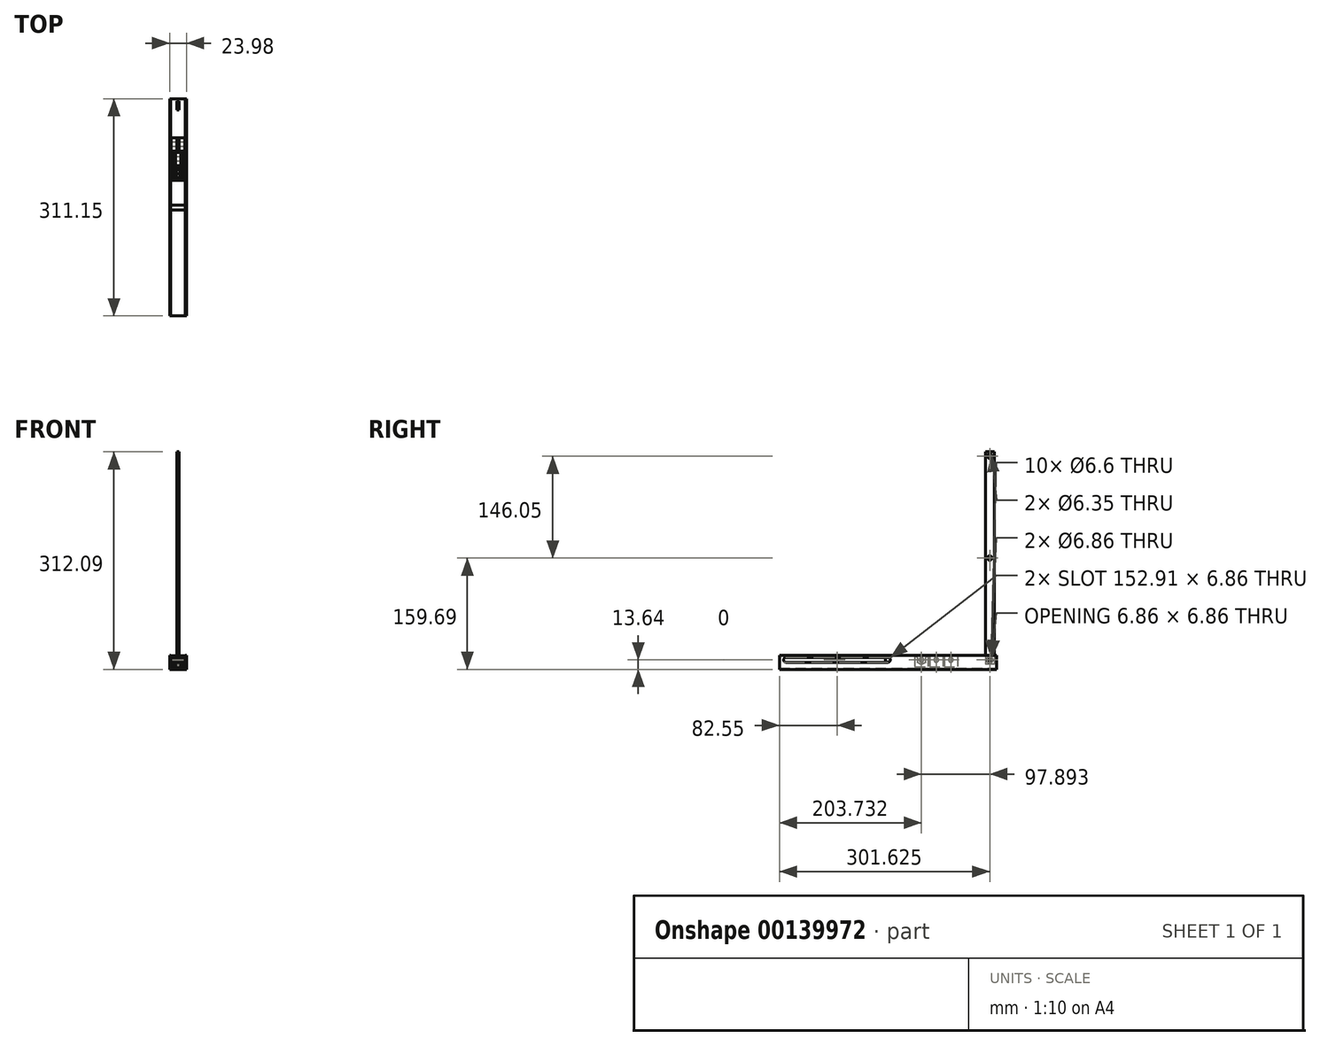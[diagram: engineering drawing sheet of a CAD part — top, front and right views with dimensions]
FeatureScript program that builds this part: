
annotation { "Feature Type Name" : "Feature", "Feature Type Description" : "" }
export const myFeature = defineFeature(function(context is Context, id is Id, definition is map)
    precondition{}
    {
        {
            var Q0;
            Q0=qCreatedBy(makeId("Front.planeOp"),FACE);
            var sketch = newSketch(context, id + "F0", { "sketchPlane" : qUnion([Q0])});
            skLineSegment(sketch, "E0", {"start": v(-11.99, 0) * mm, "end": v(11.99, 0) * mm});
            skLineSegment(sketch, "E1", {"start": v(11.99, 0) * mm, "end": v(11.99, 19.99) * mm});
            skLineSegment(sketch, "E2", {"start": v(11.99, 19.99) * mm, "end": v(10.31, 19.99) * mm});
            skLineSegment(sketch, "E3", {"start": v(10.31, 19.99) * mm, "end": v(10.31, 1.68) * mm});
            skLineSegment(sketch, "E4", {"start": v(10.31, 1.68) * mm, "end": v(-10.31, 1.68) * mm});
            skLineSegment(sketch, "E5", {"start": v(-10.31, 1.68) * mm, "end": v(-10.31, 19.99) * mm});
            skLineSegment(sketch, "E6", {"start": v(-10.31, 19.99) * mm, "end": v(-11.99, 19.99) * mm});
            skLineSegment(sketch, "E7", {"start": v(-11.99, 19.99) * mm, "end": v(-11.99, 0) * mm});
            skLineSegment(sketch, "E8", {"start": v(0, 0) * mm, "end": v(0, 10.38) * mm, "construction": true});
            skSolve(sketch);
        }
        {
            var Q0;
            Q0 = qSketchRegion(id + "F0", true);
            extrude(context, id + "F1", {"entities" : qUnion([Q0]), "depth" : 311.15 * mm});
        }
        {
            var Q0;
            Q0=qCreatedBy(makeId("Right.planeOp"),FACE);
            var sketch = newSketch(context, id + "F2", { "sketchPlane" : qUnion([Q0])});
            skCircle(sketch, "E9", {"center": v(-9.53, 13.64) * mm, "radius": 3.43 * mm});
            skArc(sketch, "E10", {"start": v(-155.58, 10.21) * mm, "mid": v(-152.15, 13.66) * mm, "end": v(-155.62, 17.07) * mm});
            skArc(sketch, "E11", {"start": v(-301.62, 17.07) * mm, "mid": v(-305.05, 13.64) * mm, "end": v(-301.62, 10.21) * mm});
            skLineSegment(sketch, "E12", {"start": v(-301.63, 13.64) * mm, "end": v(-155.58, 13.64) * mm, "construction": true});
            skLineSegment(sketch, "E13", {"start": v(-155.53, 17.07) * mm, "end": v(-301.62, 17.07) * mm});
            skLineSegment(sketch, "E14", {"start": v(-301.62, 10.21) * mm, "end": v(-155.58, 10.21) * mm});
            skSolve(sketch);
        }
        {
            var Q0;
            Q0 = qSketchRegion(id + "F2", true);
            extrude(context, id + "F3", {"entities" : qUnion([Q0]), "operationType" : NewBodyOperationType.REMOVE, "endBound" : BoundingType.THROUGH_ALL, "oppositeDirection" : true, "depth" : 25.4 * mm, "hasSecondDirection" : true, "secondDirectionBound" : SecondDirectionBoundingType.THROUGH_ALL, "secondDirectionOppositeDirection" : false, "secondDirectionDepth" : 25.4 * mm});
        }
        {
            var Q0;
            Q0=makeQuery(id+"F1.opExtrude","CAP_FACE",FACE,{"disambiguationData":[OSD([sQuery(id+"F0.wireOp",EDGE,"E0"),sQuery(id+"F0.wireOp",EDGE,"E1"),sQuery(id+"F0.wireOp",EDGE,"E2"),sQuery(id+"F0.wireOp",EDGE,"E3"),sQuery(id+"F0.wireOp",EDGE,"E4"),sQuery(id+"F0.wireOp",EDGE,"E5"),sQuery(id+"F0.wireOp",EDGE,"E6"),sQuery(id+"F0.wireOp",EDGE,"E7")])],"isStart":true});
            var sketch = newSketch(context, id + "F4", { "sketchPlane" : qUnion([Q0])});
            skLineSegment(sketch, "E15.0", {"start": v(9.8, 2.18) * mm, "end": v(9.8, 19.99) * mm});
            skLineSegment(sketch, "E15.1", {"start": v(-9.8, 2.18) * mm, "end": v(9.8, 2.18) * mm});
            skLineSegment(sketch, "E15.2", {"start": v(-9.8, 19.99) * mm, "end": v(-9.8, 2.18) * mm});
            skLineSegment(sketch, "E16", {"start": v(-9.8, 19.48) * mm, "end": v(9.8, 19.48) * mm});
            skLineSegment(sketch, "E17", {"start": v(-10.31, 19.99) * mm, "end": v(-9.8, 19.99) * mm});
            skLineSegment(sketch, "E18.trimOffspring", {"start": v(9.8, 19.99) * mm, "end": v(10.31, 19.99) * mm});
            skLineSegment(sketch, "E19", {"start": v(0, 3.7) * mm, "end": v(0, 19.48) * mm});
            skPoint(sketch, "E19.startSnap0", {"position": v(0, 19.48) * mm});
            skLineSegment(sketch, "E20", {"start": v(5.46, 19.48) * mm, "end": v(5.46, 3.7) * mm});
            skLineSegment(sketch, "E21", {"start": v(5.46, 3.7) * mm, "end": v(-5.46, 3.7) * mm});
            skLineSegment(sketch, "E22", {"start": v(-5.46, 3.7) * mm, "end": v(-5.46, 19.48) * mm});
            skLineSegment(sketch, "E23.bottom", {"start": v(-3.8, 19.48) * mm, "end": v(-7.11, 19.48) * mm});
            skLineSegment(sketch, "E23.top", {"start": v(-3.8, 3.7) * mm, "end": v(-7.11, 3.7) * mm});
            skLineSegment(sketch, "E23.left", {"start": v(-3.8, 19.48) * mm, "end": v(-3.8, 3.7) * mm});
            skLineSegment(sketch, "E23.right", {"start": v(-7.11, 19.48) * mm, "end": v(-7.11, 3.7) * mm});
            skPoint(sketch, "E23.middle", {"position": v(-5.46, 11.6) * mm});
            skLineSegment(sketch, "E24.bottom", {"start": v(-1.65, 19.48) * mm, "end": v(1.65, 19.48) * mm});
            skLineSegment(sketch, "E24.top", {"start": v(-1.65, 3.7) * mm, "end": v(1.65, 3.7) * mm});
            skLineSegment(sketch, "E24.left", {"start": v(-1.65, 19.48) * mm, "end": v(-1.65, 3.7) * mm});
            skLineSegment(sketch, "E24.right", {"start": v(1.65, 19.48) * mm, "end": v(1.65, 3.7) * mm});
            skPoint(sketch, "E24.middle", {"position": v(0, 11.6) * mm});
            skLineSegment(sketch, "E25.bottom", {"start": v(3.81, 19.48) * mm, "end": v(7.11, 19.48) * mm});
            skLineSegment(sketch, "E25.top", {"start": v(3.81, 3.7) * mm, "end": v(7.11, 3.7) * mm});
            skLineSegment(sketch, "E25.left", {"start": v(3.81, 19.48) * mm, "end": v(3.81, 3.7) * mm});
            skLineSegment(sketch, "E25.right", {"start": v(7.11, 19.48) * mm, "end": v(7.11, 3.7) * mm});
            skPoint(sketch, "E25.middle", {"position": v(5.46, 11.6) * mm});
            skSolve(sketch);
        }
        {
            var Q0;
            {var subQ0=sQuery(id+"F4.wireOp",EDGE,"E23.left");Q0=makeQuery(id+"F4.imprint","IMPRINT",FACE,{"disambiguationData":[TD([[makeQuery(id+"F4.imprint","IMPRINT",EDGE,{"derivedFrom":subQ0}),1.0]])]});}
            var Q1;
            {var subQ13=sQuery(id+"F4.wireOp",EDGE,"E15.1");Q1=makeQuery(id+"F4.imprint","IMPRINT",FACE,{"disambiguationData":[TD([[makeQuery(id+"F4.imprint","IMPRINT",EDGE,{"derivedFrom":subQ13}),1.0]])]});}
            var Q2;
            {var subQ0=sQuery(id+"F4.wireOp",EDGE,"E24.right");Q2=makeQuery(id+"F4.imprint","IMPRINT",FACE,{"disambiguationData":[TD([[makeQuery(id+"F4.imprint","IMPRINT",EDGE,{"derivedFrom":subQ0}),1.0]])]});}
            extrude(context, id + "F5", {"entities" : qUnion([Q0, Q1, Q2]), "oppositeDirection" : true, "depth" : 19.05 * mm});
        }
        {
            var Q0;
            Q0=makeQuery(id+"F5.opExtrude","SWEPT_FACE",FACE,{"disambiguationData":[OSD([sQuery(id+"F4.wireOp",EDGE,"E15.0")])]});
            var sketch = newSketch(context, id + "F6", { "sketchPlane" : qUnion([Q0])});
            skCircle(sketch, "E26", {"center": v(9.53, 13.64) * mm, "radius": 3.3 * mm});
            skSolve(sketch);
        }
        {
            var Q0;
            Q0 = qSketchRegion(id + "F6", true);
            extrude(context, id + "F7", {"entities" : qUnion([Q0]), "operationType" : NewBodyOperationType.REMOVE, "oppositeDirection" : true, "depth" : 25.4 * mm});
        }
        {
            var Q0;
            Q0=qCreatedBy(makeId("Right.planeOp"),FACE);
            var sketch = newSketch(context, id + "F8", { "sketchPlane" : qUnion([Q0])});
            skCircle(sketch, "E27.0", {"center": v(-9.53, 13.64) * mm, "radius": 3.3 * mm});
            skCircle(sketch, "E28.cCircle", {"center": v(-9.53, 13.64) * mm, "radius": 5.84 * mm, "construction": true});
            skLineSegment(sketch, "E28.0", {"start": v(-9.53, 6.9) * mm, "end": v(-15.37, 10.27) * mm});
            skLineSegment(sketch, "E28.1", {"start": v(-15.37, 10.27) * mm, "end": v(-15.37, 17.01) * mm});
            skLineSegment(sketch, "E28.2", {"start": v(-15.37, 17.01) * mm, "end": v(-9.53, 20.39) * mm});
            skLineSegment(sketch, "E28.3", {"start": v(-9.53, 20.39) * mm, "end": v(-3.68, 17.01) * mm});
            skLineSegment(sketch, "E28.4", {"start": v(-3.68, 17.01) * mm, "end": v(-3.68, 10.27) * mm});
            skLineSegment(sketch, "E28.5", {"start": v(-3.68, 10.27) * mm, "end": v(-9.53, 6.9) * mm});
            skPoint(sketch, "E28.0.midPoint", {"position": v(-12.45, 8.58) * mm});
            skLineSegment(sketch, "E29", {"start": v(-9.53, 20.39) * mm, "end": v(-9.53, 6.9) * mm});
            skLineSegment(sketch, "E30", {"start": v(-3.68, 17.01) * mm, "end": v(-3.68, 20.39) * mm});
            skLineSegment(sketch, "E31", {"start": v(-3.68, 20.39) * mm, "end": v(-15.37, 20.39) * mm});
            skLineSegment(sketch, "E32", {"start": v(-15.37, 20.39) * mm, "end": v(-15.37, 17.01) * mm});
            skSolve(sketch);
        }
        {
            var Q0;
            Q0 = qSketchRegion(id + "F8", true);
            extrude(context, id + "F9", {"entities" : qUnion([Q0]), "operationType" : NewBodyOperationType.REMOVE, "oppositeDirection" : true, "depth" : 2.54 * mm, "hasSecondDirection" : true, "secondDirectionOppositeDirection" : false, "secondDirectionDepth" : 2.54 * mm});
        }
        {
            var Q0;
            Q0=qCreatedBy(makeId("Right.planeOp"),FACE);
            var sketch = newSketch(context, id + "F10", { "sketchPlane" : qUnion([Q0])});
            skCircle(sketch, "E33.0", {"center": v(-9.53, 13.64) * mm, "radius": 3.3 * mm});
            skLineSegment(sketch, "E34", {"start": v(-9.53, 13.64) * mm, "end": v(-9.53, 305.74) * mm, "construction": true});
            skCircle(sketch, "E35", {"center": v(-9.53, 305.74) * mm, "radius": 3.18 * mm});
            skCircle(sketch, "E36", {"center": v(-9.53, 159.69) * mm, "radius": 3.18 * mm});
            skLineSegment(sketch, "E37.bottom", {"start": v(-3.18, 312.09) * mm, "end": v(-15.88, 312.09) * mm});
            skLineSegment(sketch, "E37.top", {"start": v(-3.17, 7.29) * mm, "end": v(-15.87, 7.29) * mm});
            skLineSegment(sketch, "E37.left", {"start": v(-3.18, 312.09) * mm, "end": v(-3.17, 7.29) * mm});
            skLineSegment(sketch, "E37.right", {"start": v(-15.88, 312.09) * mm, "end": v(-15.87, 7.29) * mm});
            skSolve(sketch);
        }
        {
            var Q0;
            Q0 = qSketchRegion(id + "F10", true);
            extrude(context, id + "F11", {"entities" : qUnion([Q0]), "endBound" : BoundingType.SYMMETRIC, "depth" : 3.17 * mm});
        }
        {
            var Q0;
            Q0=makeQuery(id+"F1.opExtrude","SWEPT_FACE",FACE,{"disambiguationData":[OSD([sQuery(id+"F0.wireOp",EDGE,"E7")])]});
            var sketch = newSketch(context, id + "F12", { "sketchPlane" : qUnion([Q0])});
            skCircle(sketch, "E38", {"center": v(155.62, 13.66) * mm, "radius": 3.4 * mm});
            skPoint(sketch, "E38.centerSnap0", {"position": v(152.15, 13.66) * mm});
            skSolve(sketch);
        }
        {
            var Q0;
            Q0 = qSketchRegion(id + "F12", true);
            var Q1;
            Q1=makeQuery(id+"F1.opExtrude","SWEPT_FACE",FACE,{"disambiguationData":[OSD([sQuery(id+"F0.wireOp",EDGE,"E1")])]});
            extrude(context, id + "F13", {"entities" : qUnion([Q0]), "endBound" : BoundingType.UP_TO_SURFACE, "oppositeDirection" : true, "endBoundEntityFace" : qUnion([Q1]), "depth" : 25.4 * mm});
        }
        {
            var Q0;
            Q0=makeQuery(id+"F5.opExtrude","SWEPT_BODY",BODY,{"disambiguationData":[OSD([sQuery(id+"F4.wireOp",EDGE,"E15.0"),sQuery(id+"F4.wireOp",EDGE,"E15.1"),sQuery(id+"F4.wireOp",EDGE,"E15.2"),sQuery(id+"F4.wireOp",EDGE,"E16"),sQuery(id+"F4.wireOp",EDGE,"E23.top"),sQuery(id+"F4.wireOp",EDGE,"E23.left"),sQuery(id+"F4.wireOp",EDGE,"E23.right"),sQuery(id+"F4.wireOp",EDGE,"E24.top"),sQuery(id+"F4.wireOp",EDGE,"E24.left"),sQuery(id+"F4.wireOp",EDGE,"E24.right"),sQuery(id+"F4.wireOp",EDGE,"E25.top"),sQuery(id+"F4.wireOp",EDGE,"E25.left"),sQuery(id+"F4.wireOp",EDGE,"E25.right")])]});
            transform(context, id + "F14", {"entities" : qUnion([Q0]), "transformType" : TransformType.TRANSLATION_3D, "dx" : 0 * mm, "dy" : -197.02 * mm, "dz" : 0 * mm, "makeCopy" : true});
        }
        {
            var Q0;
            Q0=makeQuery(id+"F14.opPattern","COPY",FACE,{"derivedFrom":makeQuery(id+"F5.opExtrude","SWEPT_FACE",FACE,{"disambiguationData":[OSD([sQuery(id+"F4.wireOp",EDGE,"E24.right")])]}),"instanceName":"1"});
            extrude(context, id + "F15", {"entities" : qUnion([Q0]), "operationType" : NewBodyOperationType.ADD, "endBound" : BoundingType.UP_TO_NEXT, "depth" : 25.4 * mm});
        }
        {
            var Q0;
            {var subQ0=sQuery(id+"F8.wireOp",EDGE,"E30");var subQ1=sQuery(id+"F8.wireOp",EDGE,"E28.4");var subQ2=sQuery(id+"F4.wireOp",EDGE,"E24.left");var subQ3=sQuery(id+"F4.wireOp",EDGE,"E16");var subQ4=makeQuery(id+"F9.opExtrude","SWEPT_FACE",FACE,{"disambiguationData":[OSD([subQ1,subQ0])]});var subQ5=sQuery(id+"F4.wireOp",EDGE,"E24.bottom");Q0=makeQuery(id+"F15.boolean.opBoolean","MERGE",EDGE,{"derivedFrom":[makeQuery(id+"F14.opPattern","COPY",EDGE,{"derivedFrom":makeQuery(id+"F9.boolean.opBoolean","INTERSECT",EDGE,{"derivedFrom":[makeQuery(id+"F5.opExtrude","SWEPT_FACE",FACE,{"disambiguationData":[OSD([subQ3]),TDD([makeQuery(id+"F4.imprint","IMPRINT",EDGE,{"disambiguationData":[TD([[makeQuery(id+"F4.imprint","INTERSECT",VERTEX,{"derivedFrom":[subQ3,sQuery(id+"F4.wireOp",EDGE,"E23.bottom"),sQuery(id+"F4.wireOp",EDGE,"E23.left")]}),-1.0]])],"derivedFrom":subQ3})])]}),subQ4]}),"instanceName":"1"}),makeQuery(id+"F14.opPattern","COPY",EDGE,{"derivedFrom":makeQuery(id+"F9.boolean.opBoolean","INTERSECT",EDGE,{"derivedFrom":[makeQuery(id+"F5.opExtrude","SWEPT_FACE",FACE,{"disambiguationData":[OSD([subQ3]),TDD([makeQuery(id+"F4.imprint","IMPRINT",EDGE,{"disambiguationData":[TD([[makeQuery(id+"F4.imprint","INTERSECT",VERTEX,{"derivedFrom":[subQ3,subQ5,sQuery(id+"F4.wireOp",EDGE,"E24.right")]}),-1.0]])],"derivedFrom":subQ3})])]}),subQ4]}),"instanceName":"1"}),makeQuery(id+"F15.opExtrude","SWEPT_EDGE",EDGE,{"disambiguationData":[OSD([subQ3,subQ2,subQ1,subQ0])]})]});}
            var Q1;
            {var subQ0=sQuery(id+"F8.wireOp",EDGE,"E32");var subQ1=sQuery(id+"F8.wireOp",EDGE,"E28.1");var subQ2=sQuery(id+"F4.wireOp",EDGE,"E24.left");var subQ3=sQuery(id+"F4.wireOp",EDGE,"E16");var subQ4=makeQuery(id+"F9.opExtrude","SWEPT_FACE",FACE,{"disambiguationData":[OSD([subQ1,subQ0])]});var subQ5=sQuery(id+"F4.wireOp",EDGE,"E24.bottom");Q1=makeQuery(id+"F15.boolean.opBoolean","MERGE",EDGE,{"derivedFrom":[makeQuery(id+"F14.opPattern","COPY",EDGE,{"derivedFrom":makeQuery(id+"F9.boolean.opBoolean","INTERSECT",EDGE,{"derivedFrom":[makeQuery(id+"F5.opExtrude","SWEPT_FACE",FACE,{"disambiguationData":[OSD([subQ3]),TDD([makeQuery(id+"F4.imprint","IMPRINT",EDGE,{"disambiguationData":[TD([[makeQuery(id+"F4.imprint","INTERSECT",VERTEX,{"derivedFrom":[subQ3,sQuery(id+"F4.wireOp",EDGE,"E23.bottom"),sQuery(id+"F4.wireOp",EDGE,"E23.left")]}),-1.0]])],"derivedFrom":subQ3})])]}),subQ4]}),"instanceName":"1"}),makeQuery(id+"F14.opPattern","COPY",EDGE,{"derivedFrom":makeQuery(id+"F9.boolean.opBoolean","INTERSECT",EDGE,{"derivedFrom":[makeQuery(id+"F5.opExtrude","SWEPT_FACE",FACE,{"disambiguationData":[OSD([subQ3]),TDD([makeQuery(id+"F4.imprint","IMPRINT",EDGE,{"disambiguationData":[TD([[makeQuery(id+"F4.imprint","INTERSECT",VERTEX,{"derivedFrom":[subQ3,subQ5,sQuery(id+"F4.wireOp",EDGE,"E24.right")]}),-1.0]])],"derivedFrom":subQ3})])]}),subQ4]}),"instanceName":"1"}),makeQuery(id+"F15.opExtrude","SWEPT_EDGE",EDGE,{"disambiguationData":[OSD([subQ3,subQ2,subQ1,subQ0])]})]});}
            chamfer(context, id + "F16", {"entities" : qUnion([Q0, Q1]), "width" : 2.54 * mm, "tangentPropagation" : true});
        }
        {
            var Q0;
            Q0=makeQuery(id+"F9.boolean.opBoolean","COPY",FACE,{"derivedFrom":makeQuery(id+"F9.opExtrude","CAP_FACE",FACE,{"disambiguationData":[OSD([sQuery(id+"F8.wireOp",EDGE,"E27.0"),sQuery(id+"F8.wireOp",EDGE,"E28.0"),sQuery(id+"F8.wireOp",EDGE,"E28.1"),sQuery(id+"F8.wireOp",EDGE,"E28.4"),sQuery(id+"F8.wireOp",EDGE,"E28.5"),sQuery(id+"F8.wireOp",EDGE,"E30"),sQuery(id+"F8.wireOp",EDGE,"E31"),sQuery(id+"F8.wireOp",EDGE,"E32")])],"isStart":true})});
            var Q1;
            Q1=makeQuery(id+"F5.opExtrude","SWEPT_FACE",FACE,{"disambiguationData":[OSD([sQuery(id+"F4.wireOp",EDGE,"E24.left")])]});
            extrude(context, id + "F17", {"entities" : qUnion([Q0]), "operationType" : NewBodyOperationType.ADD, "endBound" : BoundingType.UP_TO_SURFACE, "endBoundEntityFace" : qUnion([Q1]), "depth" : 25.4 * mm});
        }
        {
            var Q0;
            Q0=makeQuery(id+"F9.boolean.opBoolean","COPY",FACE,{"derivedFrom":makeQuery(id+"F9.opExtrude","CAP_FACE",FACE,{"disambiguationData":[OSD([sQuery(id+"F8.wireOp",EDGE,"E27.0"),sQuery(id+"F8.wireOp",EDGE,"E28.0"),sQuery(id+"F8.wireOp",EDGE,"E28.1"),sQuery(id+"F8.wireOp",EDGE,"E28.4"),sQuery(id+"F8.wireOp",EDGE,"E28.5"),sQuery(id+"F8.wireOp",EDGE,"E30"),sQuery(id+"F8.wireOp",EDGE,"E31"),sQuery(id+"F8.wireOp",EDGE,"E32")])],"isStart":false})});
            var Q1;
            Q1=makeQuery(id+"F5.opExtrude","SWEPT_FACE",FACE,{"disambiguationData":[OSD([sQuery(id+"F4.wireOp",EDGE,"E24.right")])]});
            extrude(context, id + "F18", {"entities" : qUnion([Q0]), "operationType" : NewBodyOperationType.ADD, "endBound" : BoundingType.UP_TO_SURFACE, "endBoundEntityFace" : qUnion([Q1]), "depth" : 25.4 * mm});
        }
        {
            var Q0;
            Q0=makeQuery(id+"F5.opExtrude","SWEPT_BODY",BODY,{"disambiguationData":[OSD([sQuery(id+"F4.wireOp",EDGE,"E15.0"),sQuery(id+"F4.wireOp",EDGE,"E15.1"),sQuery(id+"F4.wireOp",EDGE,"E15.2"),sQuery(id+"F4.wireOp",EDGE,"E16"),sQuery(id+"F4.wireOp",EDGE,"E23.top"),sQuery(id+"F4.wireOp",EDGE,"E23.left"),sQuery(id+"F4.wireOp",EDGE,"E23.right"),sQuery(id+"F4.wireOp",EDGE,"E24.top"),sQuery(id+"F4.wireOp",EDGE,"E24.left"),sQuery(id+"F4.wireOp",EDGE,"E24.right"),sQuery(id+"F4.wireOp",EDGE,"E25.top"),sQuery(id+"F4.wireOp",EDGE,"E25.left"),sQuery(id+"F4.wireOp",EDGE,"E25.right")])]});
            transform(context, id + "F19", {"entities" : qUnion([Q0]), "transformType" : TransformType.TRANSLATION_3D, "dx" : 0 * mm, "dy" : -76.68 * mm, "dz" : 0 * mm, "makeCopy" : true});
        }
        {
            var Q0;
            {var subQ0=sQuery(id+"F4.wireOp",EDGE,"E24.left");Q0=makeQuery(id+"F19.opPattern","COPY",FACE,{"derivedFrom":makeQuery(id+"F17.boolean.opBoolean","MERGE",FACE,{"derivedFrom":[makeQuery(id+"F5.opExtrude","SWEPT_FACE",FACE,{"disambiguationData":[OSD([subQ0])]}),makeQuery(id+"F17.opExtrude","CAP_FACE",FACE,{"disambiguationData":[OSD([subQ0])],"isStart":false})]}),"instanceName":"1"});}
            extrude(context, id + "F20", {"entities" : qUnion([Q0]), "operationType" : NewBodyOperationType.ADD, "endBound" : BoundingType.UP_TO_NEXT, "depth" : 25.4 * mm});
        }
        {
            var Q0;
            Q0=makeQuery(id+"F5.opExtrude","SWEPT_FACE",FACE,{"disambiguationData":[OSD([sQuery(id+"F4.wireOp",EDGE,"E25.left")])]});
            extrude(context, id + "F21", {"entities" : qUnion([Q0]), "operationType" : NewBodyOperationType.ADD, "endBound" : BoundingType.UP_TO_NEXT, "depth" : 25.4 * mm});
        }
        {
            var Q0;
            Q0=makeQuery(id+"F5.opExtrude","SWEPT_FACE",FACE,{"disambiguationData":[OSD([sQuery(id+"F4.wireOp",EDGE,"E23.right")])]});
            extrude(context, id + "F22", {"entities" : qUnion([Q0]), "operationType" : NewBodyOperationType.ADD, "endBound" : BoundingType.UP_TO_NEXT, "depth" : 25.4 * mm});
        }
        {
            var Q0;
            Q0=makeQuery(id+"F14.opPattern","COPY",BODY,{"derivedFrom":makeQuery(id+"F5.opExtrude","SWEPT_BODY",BODY,{"disambiguationData":[OSD([sQuery(id+"F4.wireOp",EDGE,"E15.0"),sQuery(id+"F4.wireOp",EDGE,"E15.1"),sQuery(id+"F4.wireOp",EDGE,"E15.2"),sQuery(id+"F4.wireOp",EDGE,"E16"),sQuery(id+"F4.wireOp",EDGE,"E23.top"),sQuery(id+"F4.wireOp",EDGE,"E23.left"),sQuery(id+"F4.wireOp",EDGE,"E23.right"),sQuery(id+"F4.wireOp",EDGE,"E24.top"),sQuery(id+"F4.wireOp",EDGE,"E24.left"),sQuery(id+"F4.wireOp",EDGE,"E24.right"),sQuery(id+"F4.wireOp",EDGE,"E25.top"),sQuery(id+"F4.wireOp",EDGE,"E25.left"),sQuery(id+"F4.wireOp",EDGE,"E25.right")])]}),"instanceName":"1"});
            transform(context, id + "F23", {"entities" : qUnion([Q0]), "transformType" : TransformType.TRANSLATION_3D, "dx" : 0 * mm, "dy" : 99.13 * mm, "dz" : 0 * mm, "makeCopy" : false});
        }
        {
            var Q0;
            Q0=makeQuery(id+"F5.opExtrude","SWEPT_BODY",BODY,{"disambiguationData":[OSD([sQuery(id+"F4.wireOp",EDGE,"E15.0"),sQuery(id+"F4.wireOp",EDGE,"E15.1"),sQuery(id+"F4.wireOp",EDGE,"E15.2"),sQuery(id+"F4.wireOp",EDGE,"E16"),sQuery(id+"F4.wireOp",EDGE,"E23.top"),sQuery(id+"F4.wireOp",EDGE,"E23.left"),sQuery(id+"F4.wireOp",EDGE,"E23.right"),sQuery(id+"F4.wireOp",EDGE,"E24.top"),sQuery(id+"F4.wireOp",EDGE,"E24.left"),sQuery(id+"F4.wireOp",EDGE,"E24.right"),sQuery(id+"F4.wireOp",EDGE,"E25.top"),sQuery(id+"F4.wireOp",EDGE,"E25.left"),sQuery(id+"F4.wireOp",EDGE,"E25.right")])]});
            transform(context, id + "F24", {"entities" : qUnion([Q0]), "transformType" : TransformType.TRANSLATION_3D, "dx" : 0 * mm, "dy" : -55.75 * mm, "dz" : 0 * mm, "makeCopy" : false});
        }
    });
